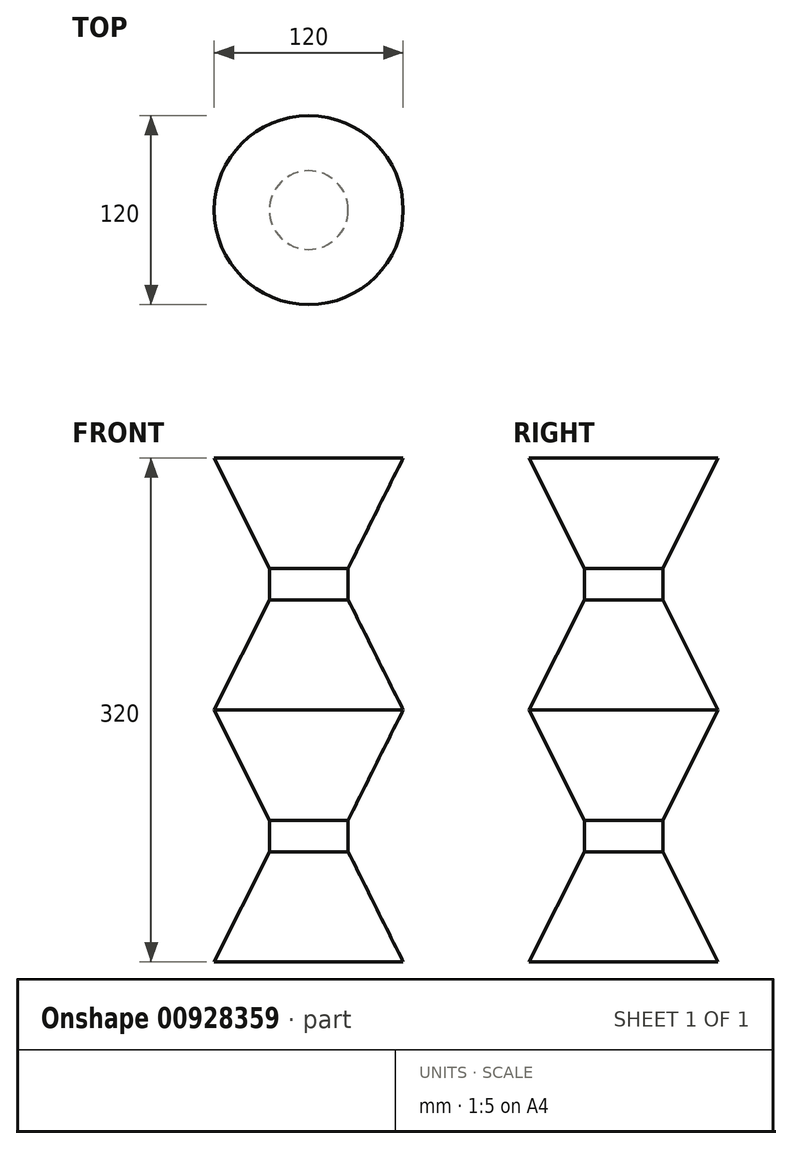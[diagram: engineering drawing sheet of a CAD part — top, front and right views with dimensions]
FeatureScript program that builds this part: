
annotation { "Feature Type Name" : "Feature", "Feature Type Description" : "" }
export const myFeature = defineFeature(function(context is Context, id is Id, definition is map)
    precondition{}
    {
        {
            var Q0;
            Q0=qCreatedBy(makeId("Top.planeOp"),FACE);
            var sketch = newSketch(context, id + "F0", { "sketchPlane" : qUnion([Q0])});
            skCircle(sketch, "E0", {"center": v(0, 0) * mm, "radius": 60 * mm});
            skSolve(sketch);
        }
        {
            var Q0;
            Q0=qCreatedBy(makeId("Top.planeOp"),FACE);
            var sketch = newSketch(context, id + "F1", { "sketchPlane" : qUnion([Q0])});
            skSolve(sketch);
        }
        {
            var Q0;
            Q0 = qBodyType(qCreatedBy(id + "F1" ,EDGE), BodyType.WIRE);
            var Q1;
            Q1=qCreatedBy(makeId("Top.planeOp"),FACE);
            cPlane(context, id + "F2", {"entities" : qUnion([Q0, Q1]), "cplaneType" : CPlaneType.OFFSET, "offset" : 70 * mm, "width" : 150 * mm, "height" : 150 * mm});
        }
        {
            var Q0;
            Q0=qCreatedBy(id+"F2.planeOp",FACE);
            var sketch = newSketch(context, id + "F3", { "sketchPlane" : qUnion([Q0])});
            skCircle(sketch, "E1", {"center": v(0, 0) * mm, "radius": 25 * mm});
            skSolve(sketch);
        }
        {
            var Q0;
            Q0=makeQuery(id+"F0.imprint","IMPRINT",FACE,{"disambiguationData":[TD([[makeQuery(id+"F0.imprint","IMPRINT",EDGE,{"derivedFrom":sQuery(id+"F0.wireOp",EDGE,"E0")}),1.0]])]});
            var Q1;
            Q1=makeQuery(id+"F3.imprint","IMPRINT",FACE,{"disambiguationData":[TD([[makeQuery(id+"F3.imprint","IMPRINT",EDGE,{"derivedFrom":sQuery(id+"F3.wireOp",EDGE,"E1")}),1.0]])]});
            loft(context, id + "F4", {"sheetProfilesArray" : [{ "sheetProfileEntities" : qUnion([Q0]) }, { "sheetProfileEntities" : qUnion([Q1]) }]});
        }
        {
            var Q0;
            Q0=makeQuery(id+"F4.opLoft","CAP_FACE",FACE,{"disambiguationData":[OSD([makeQuery(id+"F3.imprint","IMPRINT",FACE,{"disambiguationData":[TD([[makeQuery(id+"F3.imprint","IMPRINT",EDGE,{"derivedFrom":sQuery(id+"F3.wireOp",EDGE,"E1")}),1.0]])]})])],"isStart":true});
            extrude(context, id + "F5", {"entities" : qUnion([Q0]), "operationType" : NewBodyOperationType.ADD, "depth" : 10 * mm, "offsetDistance" : 25 * mm});
        }
        {
            var Q0;
            Q0=makeQuery(id+"F4.opLoft","SWEPT_BODY",BODY,{"disambiguationData":[OSD([makeQuery(id+"F0.imprint","IMPRINT",FACE,{"disambiguationData":[TD([[makeQuery(id+"F0.imprint","IMPRINT",EDGE,{"derivedFrom":sQuery(id+"F0.wireOp",EDGE,"E0")}),1.0]])]}),makeQuery(id+"F3.imprint","IMPRINT",FACE,{"disambiguationData":[TD([[makeQuery(id+"F3.imprint","IMPRINT",EDGE,{"derivedFrom":sQuery(id+"F3.wireOp",EDGE,"E1")}),1.0]])]})])]});
            var Q1;
            Q1=makeQuery(id+"F5.opExtrude","CAP_FACE",FACE,{"disambiguationData":[OSD([makeQuery(id+"F3.imprint","IMPRINT",FACE,{"disambiguationData":[TD([[makeQuery(id+"F3.imprint","IMPRINT",EDGE,{"derivedFrom":sQuery(id+"F3.wireOp",EDGE,"E1")}),1.0]])]})])],"isStart":false});
            mirror(context, id + "F6", {"operationType" : NewBodyOperationType.ADD, "entities" : qUnion([Q0]), "mirrorPlane" : qUnion([Q1])});
        }
        {
            var Q0;
            Q0=makeQuery(id+"F4.opLoft","SWEPT_BODY",BODY,{"disambiguationData":[OSD([makeQuery(id+"F0.imprint","IMPRINT",FACE,{"disambiguationData":[TD([[makeQuery(id+"F0.imprint","IMPRINT",EDGE,{"derivedFrom":sQuery(id+"F0.wireOp",EDGE,"E0")}),1.0]])]}),makeQuery(id+"F3.imprint","IMPRINT",FACE,{"disambiguationData":[TD([[makeQuery(id+"F3.imprint","IMPRINT",EDGE,{"derivedFrom":sQuery(id+"F3.wireOp",EDGE,"E1")}),1.0]])]})])]});
            var Q1;
            Q1=makeQuery(id+"F4.opLoft","CAP_FACE",FACE,{"disambiguationData":[OSD([makeQuery(id+"F0.imprint","IMPRINT",FACE,{"disambiguationData":[TD([[makeQuery(id+"F0.imprint","IMPRINT",EDGE,{"derivedFrom":sQuery(id+"F0.wireOp",EDGE,"E0")}),1.0]])]})])],"isStart":true});
            mirror(context, id + "F7", {"operationType" : NewBodyOperationType.ADD, "entities" : qUnion([Q0]), "mirrorPlane" : qUnion([Q1])});
        }
    });
